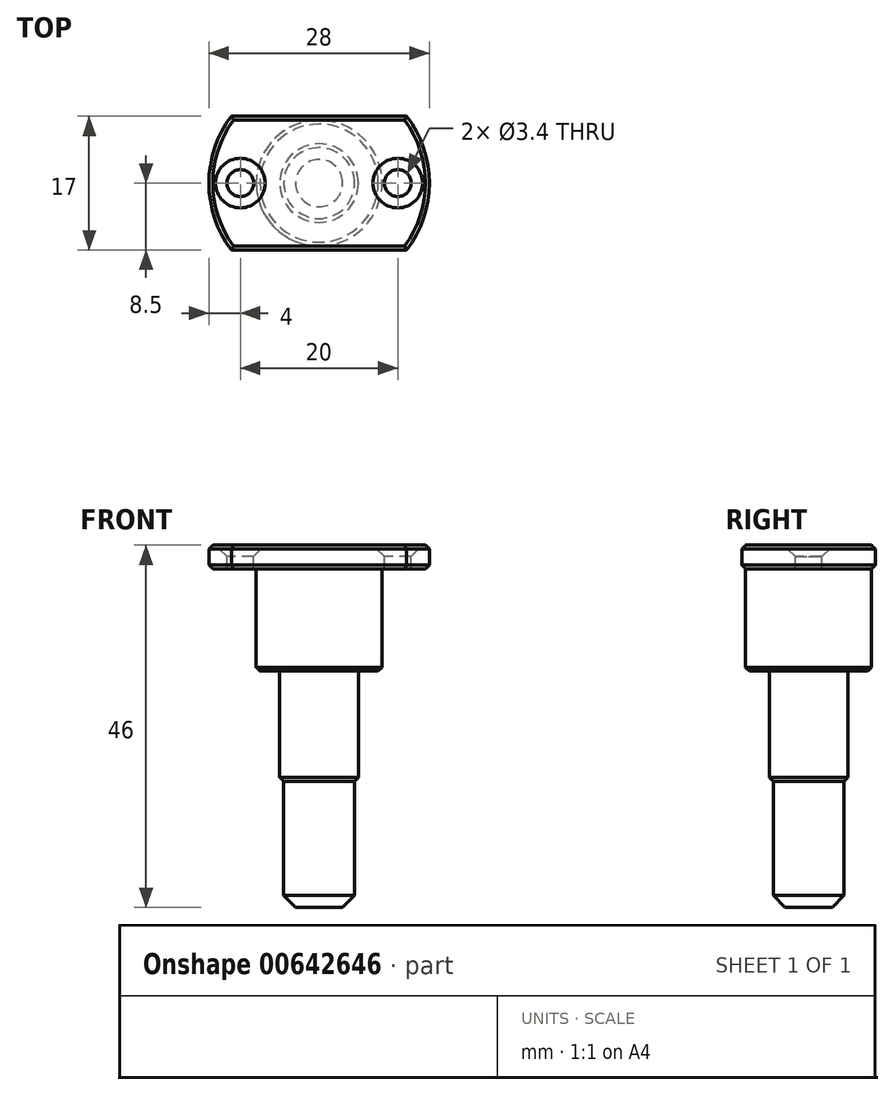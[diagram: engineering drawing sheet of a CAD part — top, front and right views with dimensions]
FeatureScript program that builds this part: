
annotation { "Feature Type Name" : "Feature", "Feature Type Description" : "" }
export const myFeature = defineFeature(function(context is Context, id is Id, definition is map)
    precondition{}
    {
        {
            var Q0;
            Q0=qCreatedBy(makeId("Top.planeOp"),FACE);
            var sketch = newSketch(context, id + "F0", { "sketchPlane" : qUnion([Q0])});
            skArc(sketch, "E0", {"start": v(-11.12, 8.5) * mm, "mid": v(-14, 0) * mm, "end": v(-11.12, -8.5) * mm});
            skLineSegment(sketch, "E1", {"start": v(-11.12, 8.5) * mm, "end": v(11.12, 8.5) * mm});
            skLineSegment(sketch, "E2.MirrorCS", {"start": v(-11.12, -8.5) * mm, "end": v(11.12, -8.5) * mm});
            skArc(sketch, "E3.trimOffspring", {"start": v(11.12, -8.5) * mm, "mid": v(14, 0) * mm, "end": v(11.12, 8.5) * mm});
            skSolve(sketch);
        }
        {
            var Q0;
            Q0 = qSketchRegion(id + "F0", true);
            extrude(context, id + "F1", {"entities" : qUnion([Q0]), "depth" : 3 * mm, "offsetDistance" : 25 * mm});
        }
        {
            var Q0;
            Q0=makeQuery(id+"F1.opExtrude","CAP_FACE",FACE,{"disambiguationData":[OSD([sQuery(id+"F0.wireOp",EDGE,"E0"),sQuery(id+"F0.wireOp",EDGE,"E1"),sQuery(id+"F0.wireOp",EDGE,"E2.MirrorCS"),sQuery(id+"F0.wireOp",EDGE,"E3.trimOffspring")])],"isStart":false});
            var Q1;
            Q1=makeQuery(id+"F1.opExtrude","CAP_FACE",FACE,{"disambiguationData":[OSD([sQuery(id+"F0.wireOp",EDGE,"E0"),sQuery(id+"F0.wireOp",EDGE,"E1"),sQuery(id+"F0.wireOp",EDGE,"E2.MirrorCS"),sQuery(id+"F0.wireOp",EDGE,"E3.trimOffspring")])],"isStart":true});
            chamfer(context, id + "F2", {"entities" : qUnion([Q0, Q1]), "width" : 0.5 * mm, "tangentPropagation" : true});
        }
        {
            var Q0;
            Q0=makeQuery(id+"F1.opExtrude","CAP_FACE",FACE,{"disambiguationData":[OSD([sQuery(id+"F0.wireOp",EDGE,"E0"),sQuery(id+"F0.wireOp",EDGE,"E1"),sQuery(id+"F0.wireOp",EDGE,"E2.MirrorCS"),sQuery(id+"F0.wireOp",EDGE,"E3.trimOffspring")])],"isStart":false});
            var sketch = newSketch(context, id + "F3", { "sketchPlane" : qUnion([Q0])});
            skPoint(sketch, "E4", {"position": v(0, 0) * mm});
            skPoint(sketch, "E5", {"position": v(-10, 0) * mm});
            skPoint(sketch, "E6", {"position": v(10, 0) * mm});
            skSolve(sketch);
        }
        {
            var Q0;
            Q0=sQuery(id+"F3.wireOp",VERTEX,"E5");
            var Q1;
            Q1=sQuery(id+"F3.wireOp",VERTEX,"E6");
            var Q2;
            Q2=makeQuery(id+"F1.opExtrude","SWEPT_BODY",BODY,{"disambiguationData":[OSD([sQuery(id+"F0.wireOp",EDGE,"E0"),sQuery(id+"F0.wireOp",EDGE,"E1"),sQuery(id+"F0.wireOp",EDGE,"E2.MirrorCS"),sQuery(id+"F0.wireOp",EDGE,"E3.trimOffspring")])]});
            hole(context, id + "F4", {"style" : HoleStyle.C_SINK, "endStyle" : HoleEndStyle.THROUGH, "holeDiameter" : 3.4 * mm, "cSinkDiameter" : 6.3 * mm, "cSinkAngle" : 90 * degree, "majorDiameter" : 5 * mm, "isTappedThrough" : true, "tappedDepth" : 12 * mm, "tapClearance" : 3, "locations" : qUnion([Q0, Q1]), "scope" : qUnion([Q2])});
        }
        {
            var Q0;
            Q0=makeQuery(id+"F1.opExtrude","CAP_FACE",FACE,{"disambiguationData":[OSD([sQuery(id+"F0.wireOp",EDGE,"E0"),sQuery(id+"F0.wireOp",EDGE,"E1"),sQuery(id+"F0.wireOp",EDGE,"E2.MirrorCS"),sQuery(id+"F0.wireOp",EDGE,"E3.trimOffspring")])],"isStart":true});
            var sketch = newSketch(context, id + "F5", { "sketchPlane" : qUnion([Q0])});
            skCircle(sketch, "E7", {"center": v(0, 0) * mm, "radius": 8 * mm});
            skSolve(sketch);
        }
        {
            var Q0;
            Q0 = qSketchRegion(id + "F5", true);
            extrude(context, id + "F6", {"entities" : qUnion([Q0]), "operationType" : NewBodyOperationType.ADD, "depth" : 13 * mm, "offsetDistance" : 25 * mm});
        }
        {
            var Q0;
            Q0=makeQuery(id+"F6.opExtrude","CAP_FACE",FACE,{"disambiguationData":[OSD([sQuery(id+"F5.wireOp",EDGE,"E7")])],"isStart":false});
            var sketch = newSketch(context, id + "F7", { "sketchPlane" : qUnion([Q0])});
            skCircle(sketch, "E8", {"center": v(0, 0) * mm, "radius": 5 * mm});
            skSolve(sketch);
        }
        {
            var Q0;
            Q0=makeQuery(id+"F7.imprint","IMPRINT",FACE,{"disambiguationData":[TD([[makeQuery(id+"F7.imprint","IMPRINT",EDGE,{"derivedFrom":sQuery(id+"F7.wireOp",EDGE,"E8")}),1.0]])]});
            extrude(context, id + "F8", {"entities" : qUnion([Q0]), "operationType" : NewBodyOperationType.ADD, "depth" : (30 - 16) * mm, "offsetDistance" : 25 * mm});
        }
        {
            var Q0;
            Q0=makeQuery(id+"F8.opExtrude","CAP_FACE",FACE,{"disambiguationData":[OSD([sQuery(id+"F7.wireOp",EDGE,"E8")])],"isStart":false});
            var sketch = newSketch(context, id + "F9", { "sketchPlane" : qUnion([Q0])});
            skCircle(sketch, "E9", {"center": v(0, 0) * mm, "radius": 4.5 * mm});
            skSolve(sketch);
        }
        {
            var Q0;
            Q0=makeQuery(id+"F9.imprint","IMPRINT",FACE,{"disambiguationData":[TD([[makeQuery(id+"F9.imprint","IMPRINT",EDGE,{"derivedFrom":sQuery(id+"F9.wireOp",EDGE,"E9")}),1.0]])]});
            extrude(context, id + "F10", {"entities" : qUnion([Q0]), "operationType" : NewBodyOperationType.ADD, "depth" : (46 - 30) * mm, "offsetDistance" : 25 * mm});
        }
        {
            var Q0;
            Q0=makeQuery(id+"F10.opExtrude","CAP_FACE",FACE,{"disambiguationData":[OSD([sQuery(id+"F9.wireOp",EDGE,"E9")])],"isStart":false});
            chamfer(context, id + "F11", {"entities" : qUnion([Q0]), "width" : 1.5 * mm, "tangentPropagation" : true});
        }
        {
            var Q0;
            Q0=makeQuery(id+"F8.opExtrude","CAP_EDGE",EDGE,{"disambiguationData":[OSD([sQuery(id+"F7.wireOp",EDGE,"E8")])],"isStart":false});
            var Q1;
            Q1=makeQuery(id+"F6.opExtrude","CAP_EDGE",EDGE,{"disambiguationData":[OSD([sQuery(id+"F5.wireOp",EDGE,"E7")])],"isStart":false});
            chamfer(context, id + "F12", {"entities" : qUnion([Q0, Q1]), "width" : 0.5 * mm, "tangentPropagation" : true});
        }
    });
